# Revit family: DE_MEA MEARIN PLUS_EXPERT_basic
name_source: partatom
category: Allgemeines Modell
revit_build: Autodesk Revit 2018 (Build: 20190510_1515(x64)
units: mm (PartAtom-declared; Revit-internal decimal feet)

## family parameters
Beim Laden mit Abzugskörper schneiden = Ja
Bemaßung runder Anschluss = Durchmesser verwenden
Gemeinsam genutzt = Nein
Kann Basisbauteil für Bewehrung sein = Nein
OmniClass-Nummer = 23.70.50.00
OmniClass-Titel = Liquid Waste Handling Services
Raumberechnungspunkt = Nein
Teiletyp = Normal

## types (12) — shared parameters
Ausführungsunterlagen = gemäß Zeichnung und Einzelbeschreibung
B_Modelltext = MEA Rinne
Bauelement = Entwässerungsrinnen Oberflächenwasser
Baustoff Stirnplatte = PC
Baustoff, Bettung/Fundament = Beton
Baustoff, Entwässerungsbauteil = UP-GF(grey)
Bauteil, Entwässerung = Entwässerungsrinne
Beschreibung = Universal Entwässerungssystem aus GFK für Belastungsklassen bis E600
Einbautechnologie = einschl. Fundament und Ummantelung
Hersteller = MEA Bautechnik GmbH Geschäftsbereich MEA Water Management
Hersteller und Typ - Ausschreibender gleichwertig = wie MEA Bautechnik GmbH, Modell MEARIN +/Expert
IfcDescription = Universal Entwässerungssystem aus GFK für Belastungsklassen bis E600
IfcExportAs = IfcWasteTerminalType
IfcExportType = USERDEFINED
Konstruktion Entwässerungsbauteil = Kastenrinne, U-Querschnitt
Rosteinlagetiefe = 20 mm  [stored 0.0656168 ft]
Typ Entwässerungsbauteil = Typ M
URL = https://www.mea-group.com
guid = cf6c1bd8-9bf4-4563-8c57-07955e2378ac

## per-type parameters (varying)
| type | Ablaufstutzen2_innendurchmesser | Ablaufstutzen3_Innendurchmesser | Ablaufstutzen_Innendurchmesser | Abstand_waag_Stutzen | Abstand_waag_Stutzen2 | Außendurchmesser Ablaufstutzen | Außendurchmesser Ablaufstutzen 2 | Außendurchmesser Ablaufstutzen 3 | B_NW | B_Stutzenlänge | Baustoff, Einlaufkasten | Baustoff, Kante | Höhe Ablaufstutzen | Höhe Ablaufstutzen 2 | Höhe Ablaufstutzen 3 | Kantenstärke | MEA-Kante | MEA-Nennweite mm | Modell | Nennweite | Nennweite mm Entwässerungsbauteil | Rinnenkörper Breite | Rinnenkörper Höhe |
| MEARIN Plus3000 - NW300 | 192 mm  [stored 0.629921 ft] | 192 mm  [stored 0.629921 ft] | 192 mm  [stored 0.629921 ft] | 100 mm  [stored 0.328084 ft] | 350 mm | 200 mm  [stored 0.656168 ft] | 200 mm  [stored 0.656168 ft] | 200 mm  [stored 0.656168 ft] | 300 | 150 mm  [stored 0.492126 ft] | Polymerbeton | Stahl, verzinkt | 755 mm | 755 mm | 755 mm | 4 mm  [stored 0.0131234 ft] | Stahl verzinkt | 300 | MEARIN Plus 300 | 300 mm  [stored 0.984252 ft] | 300 | 336 mm  [stored 1.10236 ft] | 397 mm  [stored 1.30249 ft] |
| MEARIN Plus1500 - NW150 | 192 mm  [stored 0.629921 ft] | 152 mm  [stored 0.498688 ft] | 152 mm  [stored 0.498688 ft] | 120 mm  [stored 0.393701 ft] | 324 mm | 160 mm  [stored 0.524934 ft] | 200 mm  [stored 0.656168 ft] | 160 mm  [stored 0.524934 ft] | 150 | 77 mm | UP-GF(grey) | UP-GF(grey) | 600 mm | 383 mm | 600 mm | 6 mm  [stored 0.019685 ft] | GFK | 150 | MEARIN Plus 150 | 150 mm  [stored 0.492126 ft] | 150 | 186 mm  [stored 0.610236 ft] | 187 mm  [stored 0.613517 ft] |
| MEARIN Plus2000 - NW200 | 152 mm  [stored 0.498688 ft] | 152 mm  [stored 0.498688 ft] | 192 mm  [stored 0.629921 ft] | 134 mm | 366 mm | 200 mm  [stored 0.656168 ft] | 160 mm  [stored 0.524934 ft] | 160 mm  [stored 0.524934 ft] | 200 | 150 mm  [stored 0.492126 ft] | UP-GF(grey) | UP-GF(grey) | 620 mm  [stored 2.03412 ft] | 640 mm  [stored 2.09974 ft] | 640 mm  [stored 2.09974 ft] | 6 mm  [stored 0.019685 ft] | GFK | 200 | MEARIN Plus 200 | 200 mm  [stored 0.656168 ft] | 200 | 236 mm | 242 mm  [stored 0.793963 ft] |
| MEARIN Plus1000 - NW100 | 152 mm  [stored 0.498688 ft] | 102 mm | 102 mm | 161 mm  [stored 0.528215 ft] | 324 mm | 110 mm  [stored 0.360892 ft] | 160 mm  [stored 0.524934 ft] | 110 mm  [stored 0.360892 ft] | 100 | 150 mm  [stored 0.492126 ft] | UP-GF(grey) | UP-GF(grey) | 406 mm | 385 mm | 406 mm | 6 mm  [stored 0.019685 ft] | GFK | 100 | MEARIN Plus 100 | 100 mm  [stored 0.328084 ft] | 100 | 136 mm | 158 mm |
| MEARIN EXPERT V1000 - NW100 | 152 mm  [stored 0.498688 ft] | 102 mm | 102 mm | 161 mm  [stored 0.528215 ft] | 324 mm | 110 mm  [stored 0.360892 ft] | 160 mm  [stored 0.524934 ft] | 110 mm  [stored 0.360892 ft] | 100 | 150 mm  [stored 0.492126 ft] | UP-GF(grey) | Stahl, verzinkt | 406 mm | 385 mm | 406 mm | 4 mm  [stored 0.0131234 ft] | Stahl verzinkt | 100 | MEARIN EXPERT | 100 mm  [stored 0.328084 ft] | 100 | 132 mm  [stored 0.433071 ft] | 158 mm |
| MEARIN EXPERT V1500 - NW150 | 192 mm  [stored 0.629921 ft] | 152 mm  [stored 0.498688 ft] | 152 mm  [stored 0.498688 ft] | 120 mm  [stored 0.393701 ft] | 324 mm | 160 mm  [stored 0.524934 ft] | 200 mm  [stored 0.656168 ft] | 160 mm  [stored 0.524934 ft] | 150 | 77 mm | UP-GF(grey) | Stahl, verzinkt | 600 mm | 383 mm | 600 mm | 4 mm  [stored 0.0131234 ft] | Stahl verzinkt | 150 | MEARIN EXPERT | 150 mm  [stored 0.492126 ft] | 150 | 182 mm | 187 mm  [stored 0.613517 ft] |
| MEARIN EXPERT V2000 - NW200 | 152 mm  [stored 0.498688 ft] | 152 mm  [stored 0.498688 ft] | 192 mm  [stored 0.629921 ft] | 134 mm | 366 mm | 200 mm  [stored 0.656168 ft] | 160 mm  [stored 0.524934 ft] | 160 mm  [stored 0.524934 ft] | 200 | 150 mm  [stored 0.492126 ft] | UP-GF(grey) | Stahl, verzinkt | 620 mm  [stored 2.03412 ft] | 640 mm  [stored 2.09974 ft] | 640 mm  [stored 2.09974 ft] | 4 mm  [stored 0.0131234 ft] | Stahl verzinkt | 200 | MEARIN EXPERT | 200 mm  [stored 0.656168 ft] | 200 | 232 mm  [stored 0.761155 ft] | 242 mm  [stored 0.793963 ft] |
| MEARIN EXPERT V3000 - NW300 | 192 mm  [stored 0.629921 ft] | 192 mm  [stored 0.629921 ft] | 192 mm  [stored 0.629921 ft] | 100 mm  [stored 0.328084 ft] | 350 mm | 200 mm  [stored 0.656168 ft] | 200 mm  [stored 0.656168 ft] | 200 mm  [stored 0.656168 ft] | 300 | 150 mm  [stored 0.492126 ft] | Polymerbeton | Stahl, verzinkt | 755 mm | 755 mm | 755 mm | 4 mm  [stored 0.0131234 ft] | Stahl verzinkt | 300 | MEARIN EXPERT | 300 mm  [stored 0.984252 ft] | 300 | 336 mm  [stored 1.10236 ft] | 397 mm  [stored 1.30249 ft] |
| MEARIN EXPERT E1000 - NW100 | 152 mm  [stored 0.498688 ft] | 102 mm | 102 mm | 161 mm  [stored 0.528215 ft] | 324 mm | 110 mm  [stored 0.360892 ft] | 160 mm  [stored 0.524934 ft] | 110 mm  [stored 0.360892 ft] | 100 | 150 mm  [stored 0.492126 ft] | UP-GF(grey) | Edelstahl | 406 mm | 385 mm | 406 mm | 4 mm  [stored 0.0131234 ft] | Edelstahl | 100 | MEARIN EXPERT | 100 mm  [stored 0.328084 ft] | 100 | 132 mm  [stored 0.433071 ft] | 158 mm |
| MEARIN EXPERT E1500 - NW150 | 192 mm  [stored 0.629921 ft] | 152 mm  [stored 0.498688 ft] | 152 mm  [stored 0.498688 ft] | 120 mm  [stored 0.393701 ft] | 324 mm | 160 mm  [stored 0.524934 ft] | 200 mm  [stored 0.656168 ft] | 160 mm  [stored 0.524934 ft] | 150 | 77 mm | UP-GF(grey) | Edelstahl | 600 mm | 383 mm | 600 mm | 4 mm  [stored 0.0131234 ft] | Edelstahl | 150 | MEARIN EXPERT | 150 mm  [stored 0.492126 ft] | 150 | 182 mm | 187 mm  [stored 0.613517 ft] |
| MEARIN EXPERT E2000 - NW200 | 152 mm  [stored 0.498688 ft] | 152 mm  [stored 0.498688 ft] | 192 mm  [stored 0.629921 ft] | 134 mm | 366 mm | 200 mm  [stored 0.656168 ft] | 160 mm  [stored 0.524934 ft] | 160 mm  [stored 0.524934 ft] | 200 | 150 mm  [stored 0.492126 ft] | UP-GF(grey) | Edelstahl | 620 mm  [stored 2.03412 ft] | 640 mm  [stored 2.09974 ft] | 640 mm  [stored 2.09974 ft] | 4 mm  [stored 0.0131234 ft] | Edelstahl | 200 | MEARIN EXPERT | 200 mm  [stored 0.656168 ft] | 200 | 232 mm  [stored 0.761155 ft] | 242 mm  [stored 0.793963 ft] |
| MEARIN EXPERT E3000 - NW300 | 192 mm  [stored 0.629921 ft] | 192 mm  [stored 0.629921 ft] | 192 mm  [stored 0.629921 ft] | 100 mm  [stored 0.328084 ft] | 350 mm | 200 mm  [stored 0.656168 ft] | 200 mm  [stored 0.656168 ft] | 200 mm  [stored 0.656168 ft] | 300 | 150 mm  [stored 0.492126 ft] | Polymerbeton | Edelstahl | 755 mm | 755 mm | 755 mm | 4 mm  [stored 0.0131234 ft] | Edelstahl | 300 | MEARIN EXPERT | 300 mm  [stored 0.984252 ft] | 300 | 332 mm  [stored 1.08924 ft] | 397 mm  [stored 1.30249 ft] |

note: [stored X ft] marks values corroborated as IEEE doubles in the binary element streams (Revit-internal decimal feet)
